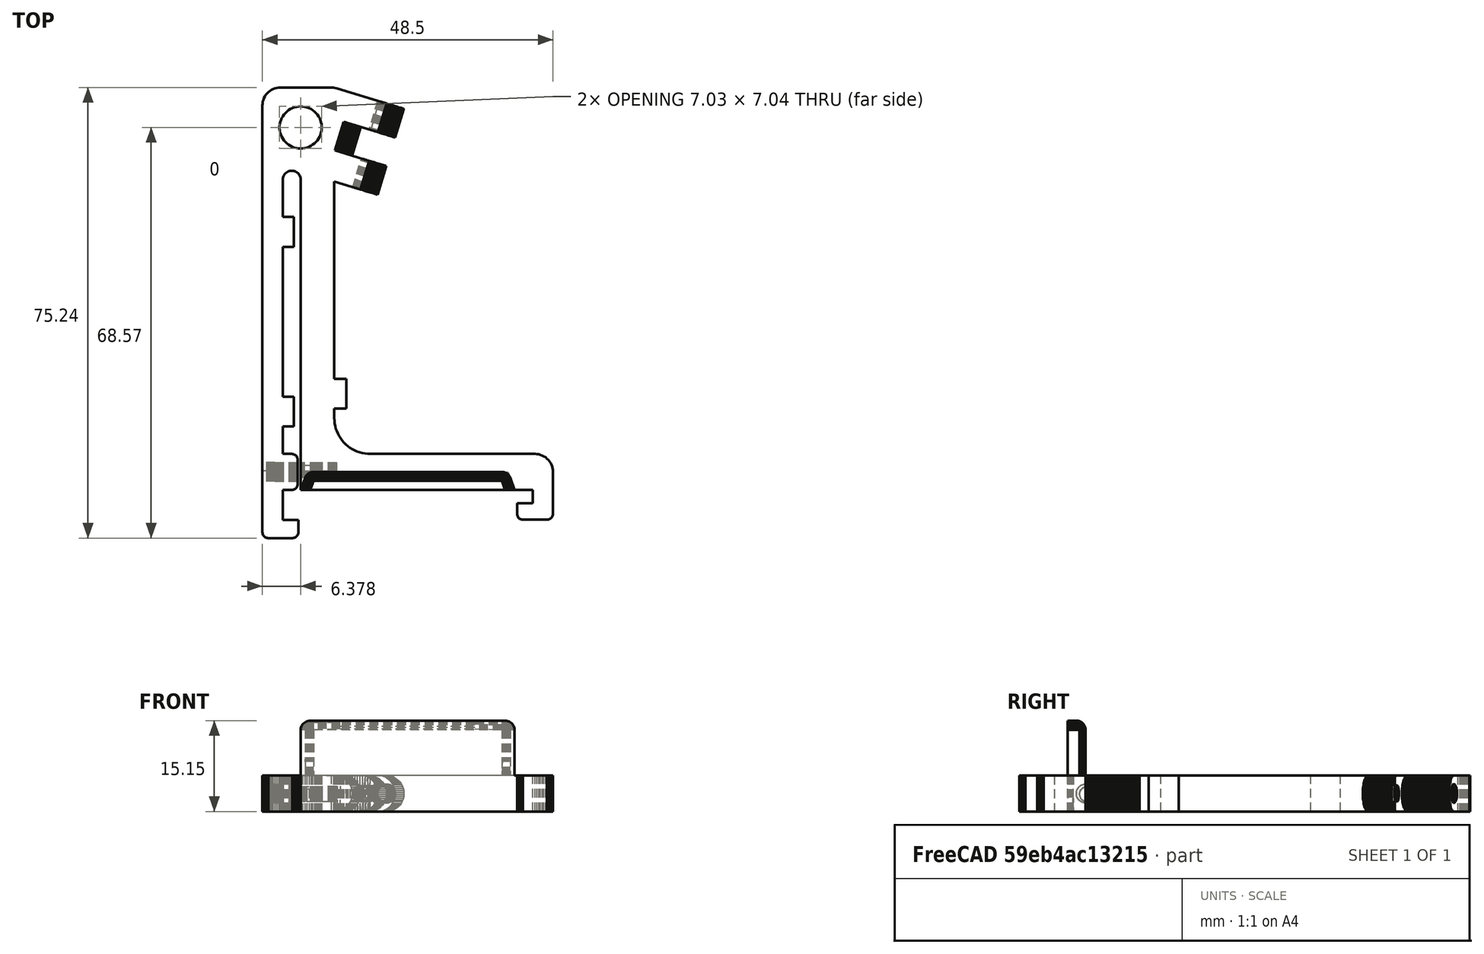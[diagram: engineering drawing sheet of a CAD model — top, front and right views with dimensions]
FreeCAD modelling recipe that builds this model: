
FCSTD DOCUMENT  (FreeCAD 0.18R14555 (Git shallow))
Label: camera-arm
License: All rights reserved
LicenseURL: http://en.wikipedia.org/wiki/All_rights_reserved
objects: Part::Feature×7, Part::Box×2, Part::MultiCommon×2, Mesh::Feature×1, Part::MultiFuse×1
note: 12 computed .brp shape members not serialized (recipe doc carries the construction recipe); baked Part::Feature solids carry a one-line shape summary decoded from their .brp

FEATURE [Mesh::Feature] Long_Bracket
FEATURE [Part::Feature] Long_Bracket001
  shape: bbox 48.5 x 75.24 x 15.15 mm, 2786 faces, 0 solids (baked)
FEATURE [Part::Feature] Long_Bracket001001  label="Long_Bracket002"
  shape: bbox 48.5 x 75.24 x 15.15 mm, 1834 faces, 0 solids (baked)
FEATURE [Part::Feature] Long_Bracket001001_solid  label="Long_Bracket002 (Solid)"
  shape: bbox 48.5 x 75.24 x 15.15 mm, 1834 faces (baked)
FEATURE [Part::Box] Box  label="Cube"
  AttacherType = Attacher::AttachEngine3D
  Height = 10
  Length = 10
  Placement = pos=(95,105,-2) rot=(0,0,1;0rad)
  Width = 5
FEATURE [Part::Feature] Long_Bracket001001_solid001  label="Long_Bracket002 (Solid)001"
  shape: bbox 48.5 x 75.24 x 15.15 mm, 1834 faces (baked)
FEATURE [Part::MultiCommon] Common
  Placement = pos=(2,-6,0) rot=(0,0,1;0rad)
  Shapes = -> [Box,Long_Bracket001001_solid]
FEATURE [Part::Box] Box001  label="Cube001"
  AttacherType = Attacher::AttachEngine3D
  Height = 10
  Length = 3
  Placement = pos=(91,105,-2) rot=(0,0,1;0rad)
  Width = 5
FEATURE [Part::Feature] Long_Bracket001001_solid002  label="Long_Bracket002 (Solid)002"
  shape: bbox 48.5 x 75.24 x 15.15 mm, 1834 faces (baked)
FEATURE [Part::MultiCommon] Common001
  Placement = pos=(2,21,0) rot=(0,0,1;0rad)
  Shapes = -> [Long_Bracket001001_solid002,Box001]
FEATURE [Part::Feature] Common001001  label="Common002"
  Placement = pos=(2,-9,0) rot=(0,0,1;0rad)
  shape: bbox 3 x 5 x 6 mm, 6 faces (baked)
FEATURE [Part::MultiFuse] Fusion
  Shapes = -> [Long_Bracket001001_solid001,Common,Common001,Common001001]
FEATURE [Part::Feature] Fusion001
  shape: bbox 48.5 x 75.24 x 15.15 mm, 1846 faces (baked)
